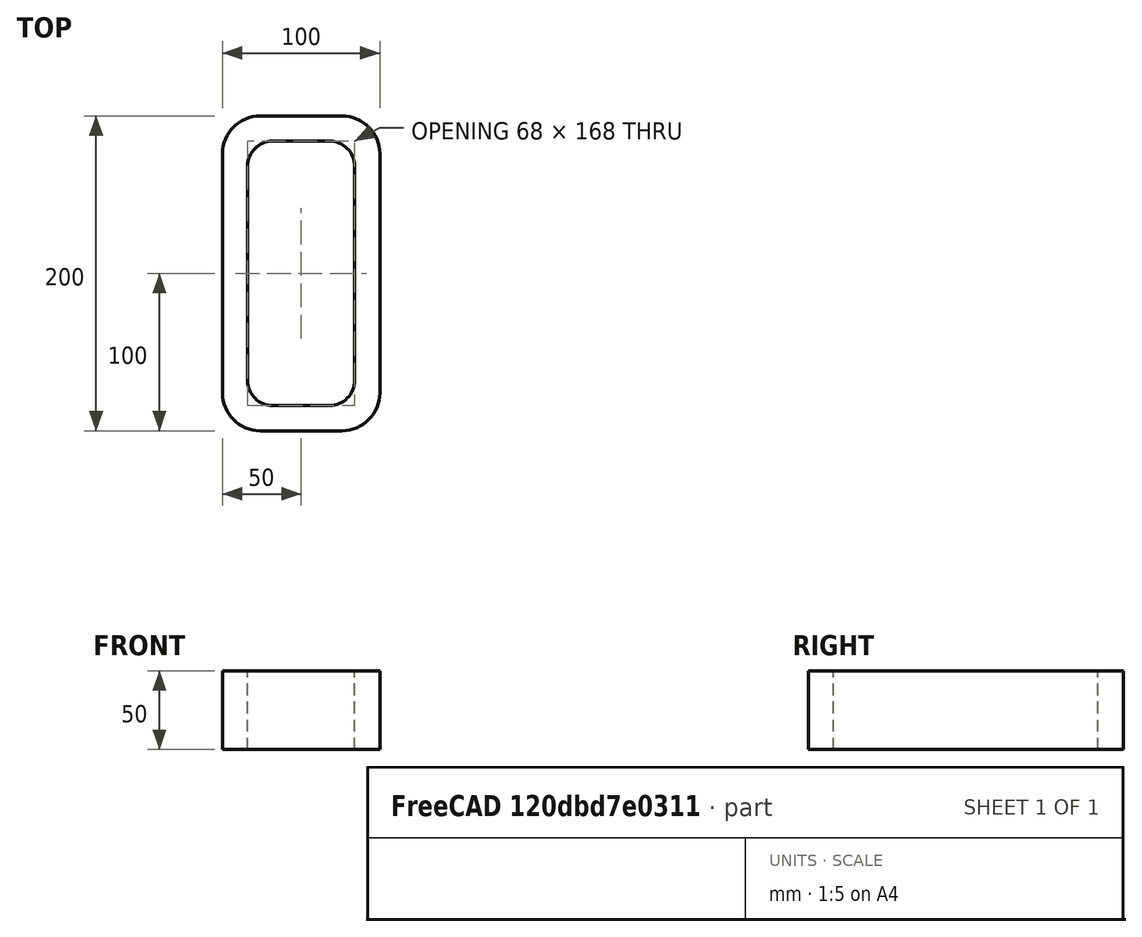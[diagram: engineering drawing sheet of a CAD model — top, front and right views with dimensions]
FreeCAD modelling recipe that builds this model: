
FCSTD DOCUMENT  (FreeCAD 0.15R4671 (Git))
Label: Rectangular hollow section 200x100x16 EN10219 S235JRH
License: All rights reserved
LicenseURL: http://en.wikipedia.org/wiki/All_rights_reserved
objects: Sketcher::SketchObject×1, Part::Extrusion×1
note: 2 computed .brp shape members not serialized (recipe doc carries the construction recipe); baked Part::Feature solids carry a one-line shape summary decoded from their .brp

FEATURE [Sketcher::SketchObject] Sketch
  sketch-geometry (16):
    g0: LineSegment StartX=-18 StartY=84 StartZ=0 EndX=18 EndY=84 EndZ=0
    g1: LineSegment StartX=34 StartY=68 StartZ=0 EndX=34 EndY=-68 EndZ=0
    g2: LineSegment StartX=18 StartY=-84 StartZ=0 EndX=-18 EndY=-84 EndZ=0
    g3: LineSegment StartX=-34 StartY=-68 StartZ=0 EndX=-34 EndY=68 EndZ=0
    g4: LineSegment StartX=-26 StartY=100 StartZ=0 EndX=26 EndY=100 EndZ=0
    g5: LineSegment StartX=50 StartY=76 StartZ=0 EndX=50 EndY=-76 EndZ=0
    g6: LineSegment StartX=26 StartY=-100 StartZ=0 EndX=-26 EndY=-100 EndZ=0
    g7: LineSegment StartX=-50 StartY=-76 StartZ=0 EndX=-50 EndY=76 EndZ=0
    g8: ArcOfCircle CenterX=-18 CenterY=68 CenterZ=0 NormalX=0 NormalY=0 NormalZ=1 Radius=16 StartAngle=1.5708 EndAngle=3.14159
    g9: ArcOfCircle CenterX=18 CenterY=68 CenterZ=0 NormalX=0 NormalY=0 NormalZ=1 Radius=16 StartAngle=0 EndAngle=1.5708
    g10: ArcOfCircle CenterX=18 CenterY=-68 CenterZ=0 NormalX=0 NormalY=0 NormalZ=1 Radius=16 StartAngle=4.71239 EndAngle=6.28319
    g11: ArcOfCircle CenterX=-18 CenterY=-68 CenterZ=0 NormalX=0 NormalY=0 NormalZ=1 Radius=16 StartAngle=3.14159 EndAngle=4.71239
    g12: ArcOfCircle CenterX=26 CenterY=76 CenterZ=0 NormalX=0 NormalY=0 NormalZ=1 Radius=24 StartAngle=0 EndAngle=1.5708
    g13: ArcOfCircle CenterX=26 CenterY=-76 CenterZ=0 NormalX=0 NormalY=0 NormalZ=1 Radius=24 StartAngle=4.71239 EndAngle=6.28319
    g14: ArcOfCircle CenterX=-26 CenterY=-76 CenterZ=0 NormalX=0 NormalY=0 NormalZ=1 Radius=24 StartAngle=3.14159 EndAngle=4.71239
    g15: ArcOfCircle CenterX=-26 CenterY=76 CenterZ=0 NormalX=0 NormalY=0 NormalZ=1 Radius=24 StartAngle=1.5708 EndAngle=3.14159
  constraints (36):
    c: Horizontal(g2)
    c: Vertical(g3)
    c: Horizontal(g6)
    c: Vertical(g7)
    c: Tangent(g3,g8) = 1.5708
    c: Tangent(g0,g8) = 1.5708
    c: Tangent(g0,g9) = 1.5708
    c: Tangent(g1,g9) = 1.5708
    c: Tangent(g1,g10) = 1.5708
    c: Tangent(g2,g10) = 1.5708
    c: Tangent(g2,g11) = 1.5708
    c: Tangent(g3,g11) = 1.5708
    c: Tangent(g4,g12) = 1.5708
    c: Tangent(g5,g12) = 1.5708
    c: Tangent(g5,g13) = 1.5708
    c: Tangent(g6,g13) = 1.5708
    c: Tangent(g6,g14) = 1.5708
    c: Tangent(g7,g14) = 1.5708
    c: Tangent(g7,g15) = 1.5708
    c: Tangent(g4,g15) = 1.5708
    c: Equal(g9,g8)
    c: Equal(g9,g11)
    c: Equal(g9,g10)
    c: Equal(g12,g15)
    c: Equal(g12,g14)
    c: Equal(g12,g13)
    c: Symmetric(g4,g6,g-1)
    c: Symmetric(g7,g5,g-2)
    c: DistanceY(g4,g6) = -200
    c: DistanceX(g7,g5) = 100
    c: Symmetric(g3,g1,g-2)
    c: Symmetric(g0,g2,g-1)
    c: DistanceY(g0,g4) = 16
    c: DistanceX(g5,g1) = -16
    c: Radius(g9) = 16
    c: Radius(g12) = 24
FEATURE [Part::Extrusion] Extrude  label="Rectangular hollow section 200x100x16 EN10219 S235JRH"
  Base = -> Sketch
  Dir = (0,0,50)
  Solid = true
